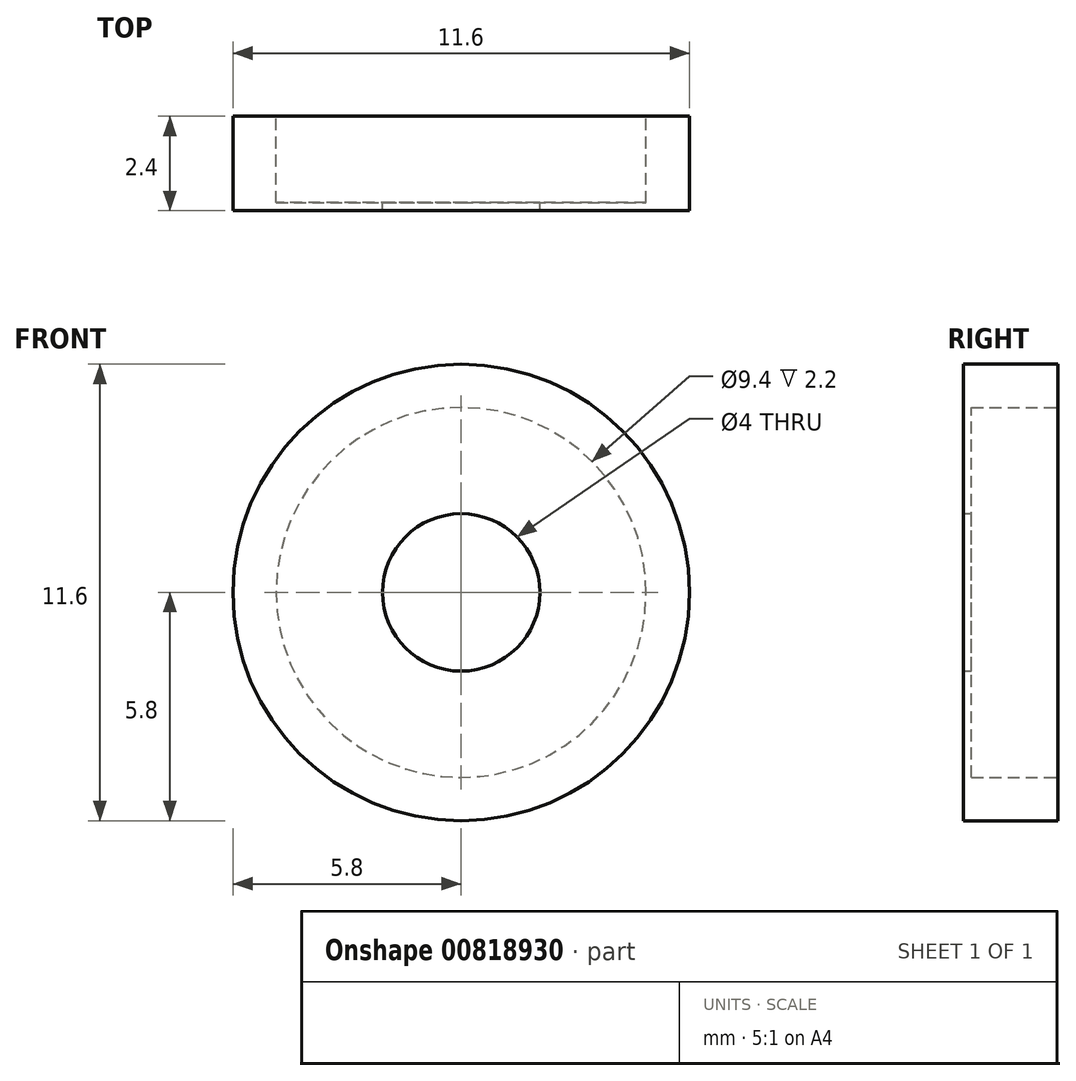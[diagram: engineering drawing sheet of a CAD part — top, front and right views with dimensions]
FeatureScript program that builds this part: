
annotation { "Feature Type Name" : "Feature", "Feature Type Description" : "" }
export const myFeature = defineFeature(function(context is Context, id is Id, definition is map)
    precondition{}
    {
        {
            var Q0;
            Q0=qCreatedBy(makeId("Front.planeOp"),FACE);
            var sketch = newSketch(context, id + "F0", { "sketchPlane" : qUnion([Q0])});
            skCircle(sketch, "E0", {"center": v(0, 0) * mm, "radius": 5.8 * mm});
            skSolve(sketch);
        }
        {
            var Q0;
            Q0=makeQuery(id+"F0.imprint","IMPRINT",FACE,{"disambiguationData":[TD([[makeQuery(id+"F0.imprint","IMPRINT",EDGE,{"derivedFrom":sQuery(id+"F0.wireOp",EDGE,"E0")}),1.0]])]});
            var Q1;
            Q1 = qSketchRegion(id + "F2", true);
            extrude(context, id + "F1", {"entities" : qUnion([Q0, Q1]), "depth" : 1.8 * mm, "offsetDistance" : 25 * mm});
        }
        {
            var Q0;
            Q0=makeQuery(id+"F1.opExtrude","CAP_FACE",FACE,{"disambiguationData":[OSD([sQuery(id+"F0.wireOp",EDGE,"E0")])],"isStart":false});
            var sketch = newSketch(context, id + "F2", { "sketchPlane" : qUnion([Q0])});
            skCircle(sketch, "E1", {"center": v(0, 0) * mm, "radius": 5.8 * mm});
            skCircle(sketch, "E2", {"center": v(0, 0) * mm, "radius": 4.7 * mm});
            skSolve(sketch);
        }
        {
            var Q0;
            Q0=makeQuery(id+"F2.imprint","IMPRINT",FACE,{"disambiguationData":[TD([[makeQuery(id+"F2.imprint","IMPRINT",EDGE,{"derivedFrom":sQuery(id+"F2.wireOp",EDGE,"E1")}),1.0]])]});
            extrude(context, id + "F3", {"entities" : qUnion([Q0]), "operationType" : NewBodyOperationType.ADD, "depth" : 0.4 * mm, "offsetDistance" : 25 * mm});
        }
        {
            var Q0;
            Q0=makeQuery(id+"F1.opExtrude","CAP_FACE",FACE,{"disambiguationData":[OSD([sQuery(id+"F0.wireOp",EDGE,"E0")])],"isStart":false});
            var sketch = newSketch(context, id + "F4", { "sketchPlane" : qUnion([Q0])});
            skCircle(sketch, "E3", {"center": v(0, 0) * mm, "radius": 4.7 * mm});
            skSolve(sketch);
        }
        {
            var Q0;
            Q0=makeQuery(id+"F4.imprint","IMPRINT",FACE,{"disambiguationData":[TD([[makeQuery(id+"F4.imprint","IMPRINT",EDGE,{"derivedFrom":sQuery(id+"F4.wireOp",EDGE,"E3")}),1.0]])]});
            extrude(context, id + "F5", {"entities" : qUnion([Q0]), "operationType" : NewBodyOperationType.REMOVE, "oppositeDirection" : true, "depth" : 1.8 * mm, "offsetDistance" : 25 * mm});
        }
        {
            var Q0;
            Q0=makeQuery(id+"F3.opExtrude","CAP_FACE",FACE,{"disambiguationData":[OSD([sQuery(id+"F2.wireOp",EDGE,"E1"),sQuery(id+"F2.wireOp",EDGE,"E2")])],"isStart":false});
            var sketch = newSketch(context, id + "F6", { "sketchPlane" : qUnion([Q0])});
            skCircle(sketch, "E4", {"center": v(0, 0) * mm, "radius": 5.8 * mm});
            skCircle(sketch, "E5", {"center": v(0, 0) * mm, "radius": 2 * mm});
            skSolve(sketch);
        }
        {
            var Q0;
            Q0=makeQuery(id+"F6.imprint","IMPRINT",FACE,{"disambiguationData":[TD([[makeQuery(id+"F6.imprint","IMPRINT",EDGE,{"derivedFrom":sQuery(id+"F6.wireOp",EDGE,"E4")}),1.0]])]});
            var Q1;
            Q1=makeQuery(id+"F6.imprint","IMPRINT",FACE,{"disambiguationData":[TD([[makeQuery(id+"F6.imprint","IMPRINT",EDGE,{"derivedFrom":sQuery(id+"F6.wireOp",EDGE,"E5")}),-1.0]])]});
            extrude(context, id + "F7", {"entities" : qUnion([Q0, Q1]), "operationType" : NewBodyOperationType.ADD, "depth" : 0.2 * mm, "offsetDistance" : 25 * mm});
        }
    });
